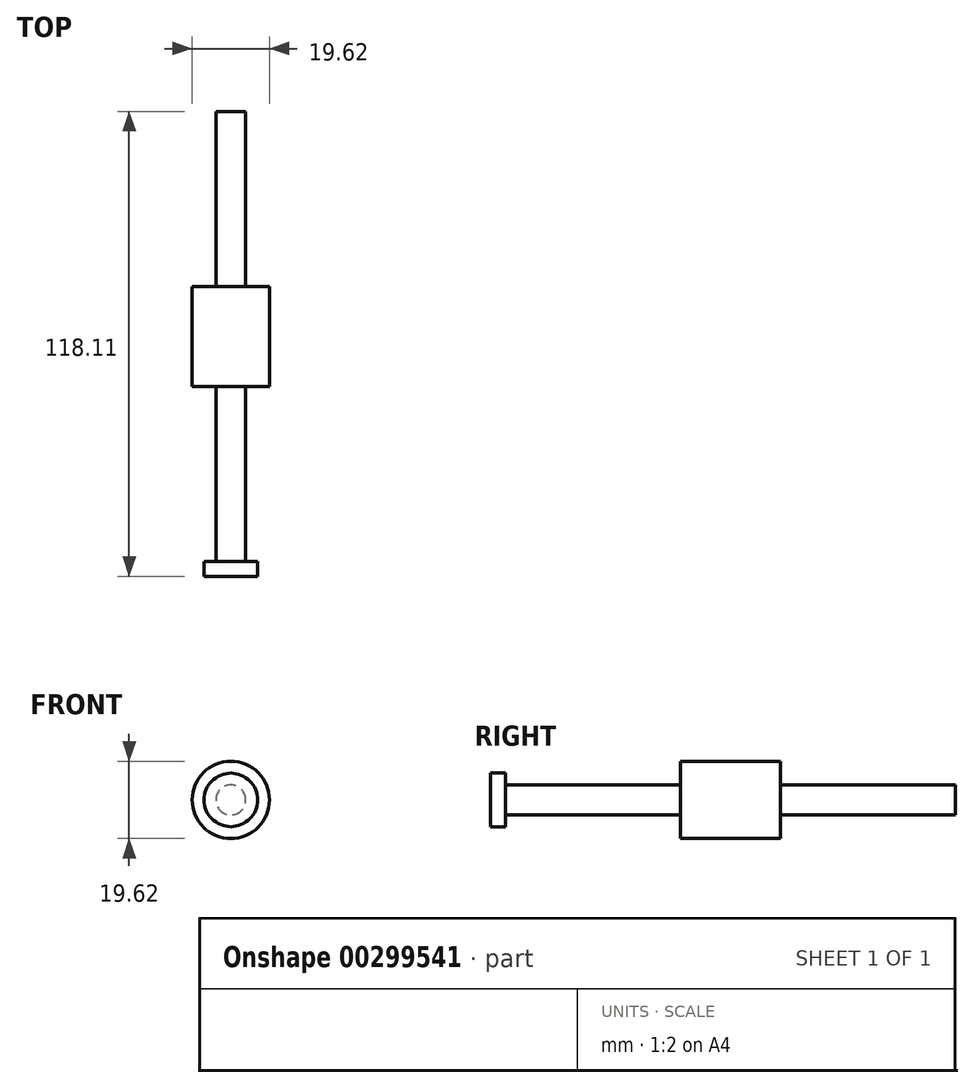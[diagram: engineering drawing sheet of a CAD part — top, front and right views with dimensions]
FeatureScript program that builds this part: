
annotation { "Feature Type Name" : "Feature", "Feature Type Description" : "" }
export const myFeature = defineFeature(function(context is Context, id is Id, definition is map)
    precondition{}
    {
        {
            var Q0;
            Q0=qCreatedBy(makeId("Front.planeOp"),FACE);
            var sketch = newSketch(context, id + "F0", { "sketchPlane" : qUnion([Q0])});
            skCircle(sketch, "E0", {"center": v(0, 0) * mm, "radius": 9.8 * mm});
            skSolve(sketch);
        }
        {
            var Q0;
            Q0 = qSketchRegion(id + "F0", true);
            extrude(context, id + "F1", {"entities" : qUnion([Q0]), "depth" : 25.4 * mm});
        }
        {
            var Q0;
            Q0=makeQuery(id+"F1.opExtrude","CAP_FACE",FACE,{"disambiguationData":[OSD([sQuery(id+"F0.wireOp",EDGE,"E0")])],"isStart":false});
            var sketch = newSketch(context, id + "F2", { "sketchPlane" : qUnion([Q0])});
            skCircle(sketch, "E1", {"center": v(0, 0) * mm, "radius": 3.8 * mm});
            skSolve(sketch);
        }
        {
            var Q0;
            Q0=makeQuery(id+"F1.opExtrude","CAP_FACE",FACE,{"disambiguationData":[OSD([sQuery(id+"F0.wireOp",EDGE,"E0")])],"isStart":true});
            var sketch = newSketch(context, id + "F3", { "sketchPlane" : qUnion([Q0])});
            skCircle(sketch, "E2", {"center": v(0, 0) * mm, "radius": 3.8 * mm});
            skSolve(sketch);
        }
        {
            var Q0;
            Q0 = qSketchRegion(id + "F3", true);
            extrude(context, id + "F4", {"entities" : qUnion([Q0]), "operationType" : NewBodyOperationType.ADD, "depth" : 44.45 * mm});
        }
        {
            var Q0;
            Q0 = qSketchRegion(id + "F0jqmMYYc6vaYRL_1", true);
            var Q1;
            Q1=makeQuery(id+"F2.imprint","IMPRINT",FACE,{"disambiguationData":[TD([[makeQuery(id+"F2.imprint","IMPRINT",EDGE,{"derivedFrom":sQuery(id+"F2.wireOp",EDGE,"E1")}),1.0]])]});
            extrude(context, id + "F5", {"entities" : qUnion([Q0, Q1]), "operationType" : NewBodyOperationType.ADD, "depth" : 44.45 * mm});
        }
        {
            var Q0;
            Q0=makeQuery(id+"F5.opExtrude","CAP_FACE",FACE,{"disambiguationData":[OSD([sQuery(id+"F2.wireOp",EDGE,"E1")])],"isStart":false});
            var sketch = newSketch(context, id + "F6", { "sketchPlane" : qUnion([Q0])});
            skCircle(sketch, "E3", {"center": v(0, 0) * mm, "radius": 6.8 * mm});
            skSolve(sketch);
        }
        {
            var Q0;
            Q0 = qSketchRegion(id + "F6", true);
            extrude(context, id + "F7", {"entities" : qUnion([Q0]), "operationType" : NewBodyOperationType.ADD, "depth" : 3.8 * mm});
        }
    });
